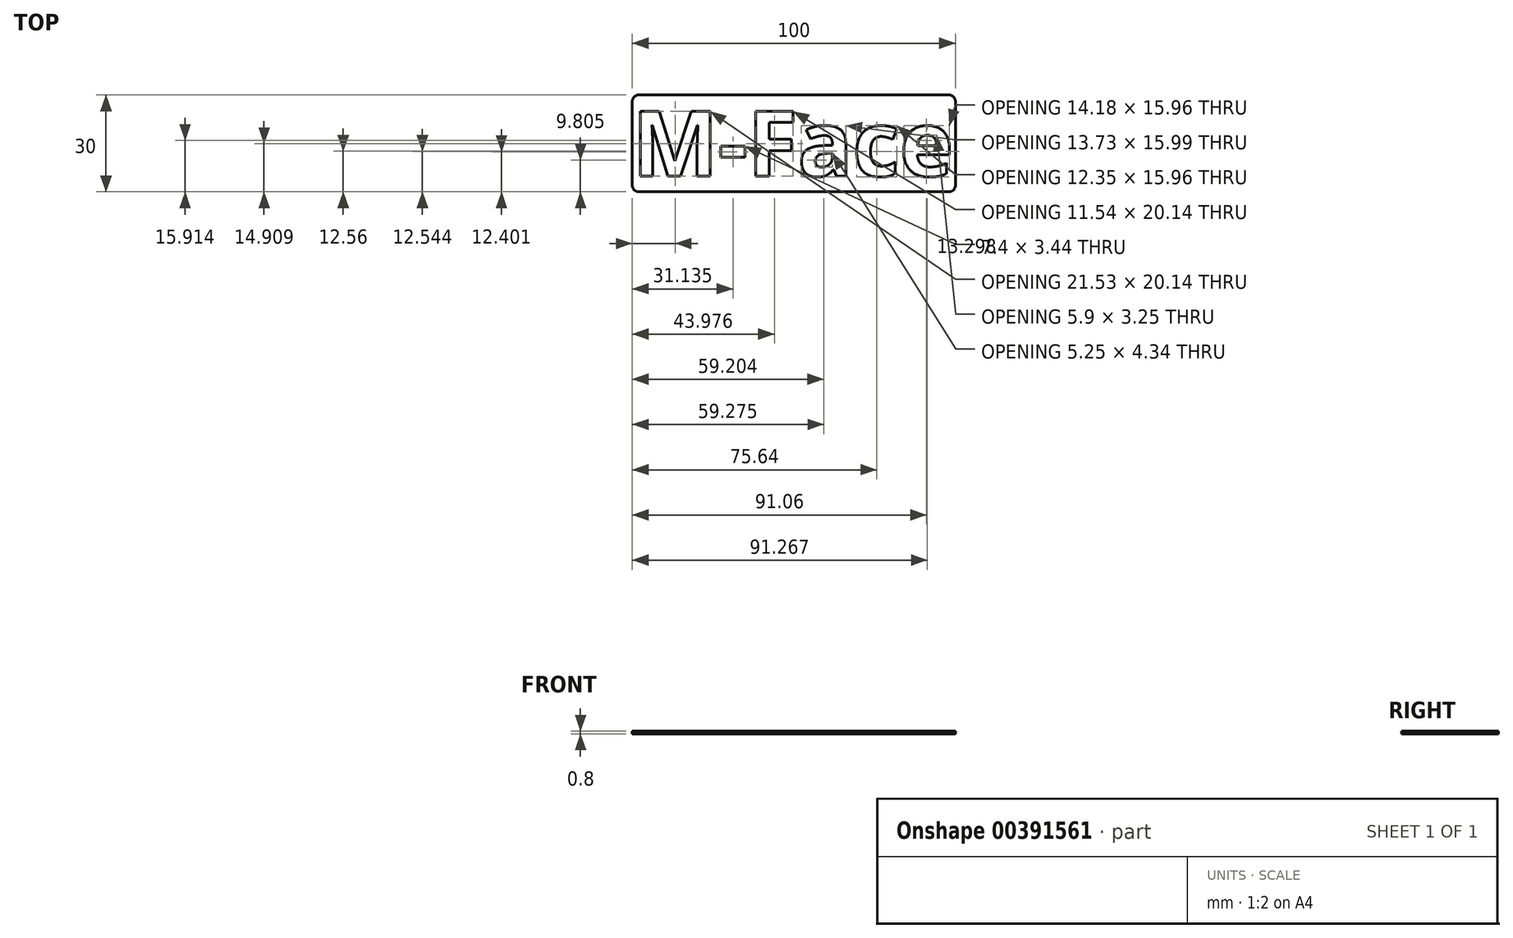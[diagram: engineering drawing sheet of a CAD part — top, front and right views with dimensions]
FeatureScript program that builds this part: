
annotation { "Feature Type Name" : "Feature", "Feature Type Description" : "" }
export const myFeature = defineFeature(function(context is Context, id is Id, definition is map)
    precondition{}
    {
        {
            var Q0;
            Q0=qCreatedBy(makeId("Top.planeOp"),FACE);
            var sketch = newSketch(context, id + "F0", { "sketchPlane" : qUnion([Q0])});
            skLineSegment(sketch, "E0.bottom", {"start": v(-50, 15) * mm, "end": v(50, 15) * mm});
            skLineSegment(sketch, "E0.top", {"start": v(-50, -15) * mm, "end": v(50, -15) * mm});
            skLineSegment(sketch, "E0.left", {"start": v(-50, 15) * mm, "end": v(-50, -15) * mm});
            skLineSegment(sketch, "E0.right", {"start": v(50, 15) * mm, "end": v(50, -15) * mm});
            skSolve(sketch);
        }
        {
            var Q0;
            Q0=makeQuery(id+"F0.imprint","IMPRINT",FACE,{"disambiguationData":[TD([[makeQuery(id+"F0.imprint","IMPRINT",EDGE,{"derivedFrom":sQuery(id+"F0.wireOp",EDGE,"E0.bottom")}),-1.0]])]});
            extrude(context, id + "F1", {"entities" : qUnion([Q0]), "depth" : 0.8 * mm});
        }
        {
            var Q0;
            Q0=makeQuery(id+"F1.opExtrude","CAP_FACE",FACE,{"disambiguationData":[OSD([sQuery(id+"F0.wireOp",EDGE,"E0.bottom"),sQuery(id+"F0.wireOp",EDGE,"E0.top"),sQuery(id+"F0.wireOp",EDGE,"E0.left"),sQuery(id+"F0.wireOp",EDGE,"E0.right")])],"isStart":false});
            var sketch = newSketch(context, id + "F2", { "sketchPlane" : qUnion([Q0])});
            skText(sketch, "E1", { "text": "M-Face", "fontName": "OpenSans-Bold.ttf"});
            const initialGuessF2  = {"E1": [-0.05, -0.01016, 1, 0, 0.02031]};
            skSetInitialGuess(sketch, initialGuessF2);
            skSolve(sketch);
        }
        {
            var Q0;
            Q0 = qSketchRegion(id + "F2", true);
            extrude(context, id + "F3", {"entities" : qUnion([Q0]), "operationType" : NewBodyOperationType.REMOVE, "oppositeDirection" : true, "depth" : 25 * mm});
        }
        {
            var Q0;
            Q0 = qSketchRegion(id + "F2", true);
            extrude(context, id + "F4", {"entities" : qUnion([Q0]), "oppositeDirection" : true, "depth" : 0.8 * mm});
        }
        {
            var Q0;
            Q0=makeQuery(id+"F1.opExtrude","SWEPT_EDGE",EDGE,{"disambiguationData":[OSD([sQuery(id+"F0.wireOp",EDGE,"E0.top"),sQuery(id+"F0.wireOp",EDGE,"E0.left")])]});
            var Q1;
            Q1=makeQuery(id+"F1.opExtrude","SWEPT_EDGE",EDGE,{"disambiguationData":[OSD([sQuery(id+"F0.wireOp",EDGE,"E0.top"),sQuery(id+"F0.wireOp",EDGE,"E0.right")])]});
            var Q2;
            Q2=makeQuery(id+"F1.opExtrude","SWEPT_EDGE",EDGE,{"disambiguationData":[OSD([sQuery(id+"F0.wireOp",EDGE,"E0.bottom"),sQuery(id+"F0.wireOp",EDGE,"E0.right")])]});
            var Q3;
            Q3=makeQuery(id+"F1.opExtrude","SWEPT_EDGE",EDGE,{"disambiguationData":[OSD([sQuery(id+"F0.wireOp",EDGE,"E0.bottom"),sQuery(id+"F0.wireOp",EDGE,"E0.left")])]});
            fillet(context, id + "F5", {"entities" : qUnion([Q0, Q1, Q2, Q3]), "radius" : 2 * mm, "tangentPropagation" : true, "allowEdgeOverflow" : false});
        }
    });
